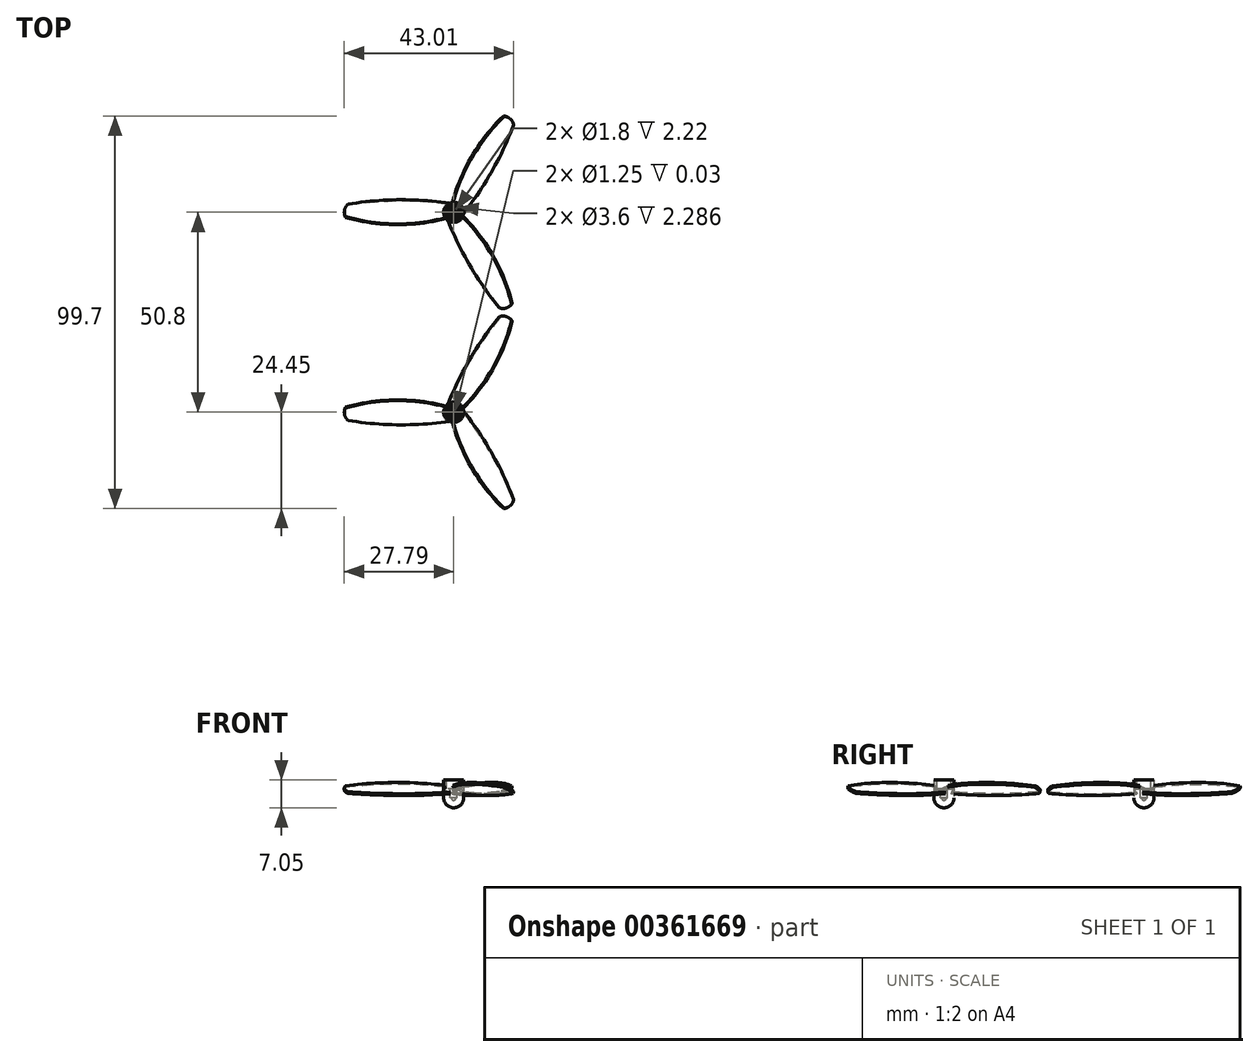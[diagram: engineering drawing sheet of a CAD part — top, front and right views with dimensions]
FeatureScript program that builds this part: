
annotation { "Feature Type Name" : "Feature", "Feature Type Description" : "" }
export const myFeature = defineFeature(function(context is Context, id is Id, definition is map)
    precondition{}
    {
        {
            var Q0;
            Q0=qCreatedBy(makeId("Top.planeOp"),FACE);
            var sketch = newSketch(context, id + "F0", { "sketchPlane" : qUnion([Q0])});
            skCircle(sketch, "E0", {"center": v(0, 0) * mm, "radius": 0.63 * mm});
            skCircle(sketch, "E1", {"center": v(0, 0) * mm, "radius": 1.5 * mm});
            skCircle(sketch, "E2.0", {"center": v(0, 0) * mm, "radius": 2.55 * mm});
            skArc(sketch, "E3", {"start": v(-1.98, 1.6) * mm, "mid": v(-14.75, 3.36) * mm, "end": v(-27.48, 1.31) * mm});
            skArc(sketch, "E4", {"start": v(-27.48, 1.31) * mm, "mid": v(-27.74, -0.54) * mm, "end": v(-26.84, -2.17) * mm});
            skArc(sketch, "E5", {"start": v(-26.84, -2.17) * mm, "mid": v(-13.84, -3.4) * mm, "end": v(-0.82, -2.42) * mm});
            skSolve(sketch);
        }
        {
            var Q0;
            Q0=makeQuery(id+"F0.imprint","IMPRINT",FACE,{"disambiguationData":[TD([[makeQuery(id+"F0.imprint","IMPRINT",EDGE,{"derivedFrom":sQuery(id+"F0.wireOp",EDGE,"E1")}),-1.0]])]});
            extrude(context, id + "F1", {"entities" : qUnion([Q0]), "endBound" : BoundingType.SYMMETRIC, "depth" : 4.5 * mm});
        }
        {
            var Q0;
            Q0=makeQuery(id+"F0.imprint","IMPRINT",FACE,{"disambiguationData":[TD([[makeQuery(id+"F0.imprint","IMPRINT",EDGE,{"derivedFrom":sQuery(id+"F0.wireOp",EDGE,"E0")}),-1.0]])]});
            extrude(context, id + "F2", {"entities" : qUnion([Q0]), "operationType" : NewBodyOperationType.ADD, "oppositeDirection" : true, "depth" : 2.25 * mm});
        }
        {
            var Q0;
            {var subQ0=sQuery(id+"F0.wireOp",EDGE,"E1");Q0=makeQuery(id+"F2.boolean.opBoolean","MERGE",FACE,{"derivedFrom":[makeQuery(id+"F1.opExtrude","CAP_FACE",FACE,{"disambiguationData":[OSD([subQ0,sQuery(id+"F0.wireOp",EDGE,"E2.0")])],"isStart":true}),makeQuery(id+"F2.opExtrude","CAP_FACE",FACE,{"disambiguationData":[OSD([sQuery(id+"F0.wireOp",EDGE,"E0"),subQ0])],"isStart":false})]});}
            var sketch = newSketch(context, id + "F3", { "sketchPlane" : qUnion([Q0])});
            skLineSegment(sketch, "E6", {"start": v(0, 2.55) * mm, "end": v(0, -2.55) * mm});
            skArc(sketch, "E7", {"start": v(0, -2.55) * mm, "mid": v(2.55, 0) * mm, "end": v(0, 2.55) * mm});
            skSolve(sketch);
        }
        {
            var Q0;
            {var subQ0=sQuery(id+"F3.wireOp",EDGE,"E7");Q0=makeQuery(id+"F3.imprint","IMPRINT",FACE,{"disambiguationData":[TD([[makeQuery(id+"F3.imprint","IMPRINT",EDGE,{"derivedFrom":subQ0}),-1.0]])]});}
            var Q1;
            Q1=sQuery(id+"F3.wireOp",EDGE,"E6");
            revolve(context, id + "F4", {"operationType" : NewBodyOperationType.ADD, "entities" : qUnion([Q0]), "axis" : qUnion([Q1]), "revolveType" : RevolveType.ONE_DIRECTION, "angle" : 180 * degree});
        }
        {
            var Q0;
            {var subQ0=sQuery(id+"F0.wireOp",EDGE,"E3");Q0=makeQuery(id+"F0.imprint","IMPRINT",FACE,{"disambiguationData":[TD([[makeQuery(id+"F0.imprint","IMPRINT",EDGE,{"derivedFrom":subQ0}),1.0]])]});}
            extrude(context, id + "F5", {"entities" : qUnion([Q0]), "endBound" : BoundingType.SYMMETRIC, "depth" : 0.5 * mm});
        }
        {
            var Q0;
            Q0=qCreatedBy(makeId("Top.planeOp"),FACE);
            var sketch = newSketch(context, id + "F6", { "sketchPlane" : qUnion([Q0])});
            skLineSegment(sketch, "E8", {"start": v(7.03, 0) * mm, "end": v(-6.93, 0) * mm});
            skSolve(sketch);
        }
        {
            var Q0;
            Q0=makeQuery(id+"F5.opExtrude","SWEPT_BODY",BODY,{"disambiguationData":[OSD([sQuery(id+"F0.wireOp",EDGE,"E2.0"),sQuery(id+"F0.wireOp",EDGE,"E3"),sQuery(id+"F0.wireOp",EDGE,"E4"),sQuery(id+"F0.wireOp",EDGE,"E5")])]});
            var Q1;
            Q1=sQuery(id+"F6.wireOp",EDGE,"E8");
            transform(context, id + "F7", {"entities" : qUnion([Q0]), "transformType" : TransformType.ROTATION, "transformAxis" : qUnion([Q1]), "angle" : 25 * degree, "oppositeDirection" : true, "makeCopy" : false});
        }
        {
            var Q0;
            Q0=makeQuery(id+"F5.opExtrude","SWEPT_BODY",BODY,{"disambiguationData":[OSD([sQuery(id+"F0.wireOp",EDGE,"E2.0"),sQuery(id+"F0.wireOp",EDGE,"E3"),sQuery(id+"F0.wireOp",EDGE,"E4"),sQuery(id+"F0.wireOp",EDGE,"E5")])]});
            var Q1;
            Q1=sQuery(id+"F0.wireOp",EDGE,"E0");
            circularPattern(context, id + "F8", {"entities" : qUnion([Q0]), "axis" : qUnion([Q1]), "angle" : 360 * degree, "instanceCount" : 3, "equalSpace" : true});
        }
        {
            var Q0;
            Q0=makeQuery(id+"F8.opPattern","COPY",BODY,{"derivedFrom":makeQuery(id+"F5.opExtrude","SWEPT_BODY",BODY,{"disambiguationData":[OSD([sQuery(id+"F0.wireOp",EDGE,"E2.0"),sQuery(id+"F0.wireOp",EDGE,"E3"),sQuery(id+"F0.wireOp",EDGE,"E4"),sQuery(id+"F0.wireOp",EDGE,"E5")])]}),"instanceName":"1"});
            var Q1;
            Q1=makeQuery(id+"F8.opPattern","COPY",BODY,{"derivedFrom":makeQuery(id+"F5.opExtrude","SWEPT_BODY",BODY,{"disambiguationData":[OSD([sQuery(id+"F0.wireOp",EDGE,"E2.0"),sQuery(id+"F0.wireOp",EDGE,"E3"),sQuery(id+"F0.wireOp",EDGE,"E4"),sQuery(id+"F0.wireOp",EDGE,"E5")])]}),"instanceName":"2"});
            var Q2;
            Q2=makeQuery(id+"F5.opExtrude","SWEPT_BODY",BODY,{"disambiguationData":[OSD([sQuery(id+"F0.wireOp",EDGE,"E2.0"),sQuery(id+"F0.wireOp",EDGE,"E3"),sQuery(id+"F0.wireOp",EDGE,"E4"),sQuery(id+"F0.wireOp",EDGE,"E5")])]});
            var Q3;
            Q3=makeQuery(id+"F1.opExtrude","SWEPT_BODY",BODY,{"disambiguationData":[OSD([sQuery(id+"F0.wireOp",EDGE,"E1"),sQuery(id+"F0.wireOp",EDGE,"E2.0")])]});
            var Q4;
            Q4=qCreatedBy(makeId("Front.planeOp"),FACE);
            transform(context, id + "F9", {"entities" : qUnion([Q0, Q1, Q2, Q3]), "transformType" : TransformType.TRANSLATION_DISTANCE, "transformDirection" : qUnion([Q4]), "distance" : 25.4 * mm, "makeCopy" : false});
        }
        {
            var Q0;
            Q0=makeQuery(id+"F1.opExtrude","CAP_FACE",FACE,{"disambiguationData":[OSD([sQuery(id+"F0.wireOp",EDGE,"E1"),sQuery(id+"F0.wireOp",EDGE,"E2.0")])],"isStart":false});
            var sketch = newSketch(context, id + "F10", { "sketchPlane" : qUnion([Q0])});
            skCircle(sketch, "E9", {"center": v(0, -25.4) * mm, "radius": 0.9 * mm});
            skCircle(sketch, "E10", {"center": v(0, -25.4) * mm, "radius": 1.8 * mm});
            skSolve(sketch);
        }
        {
            var Q0;
            Q0=makeQuery(id+"F10.imprint","IMPRINT",FACE,{"disambiguationData":[TD([[makeQuery(id+"F10.imprint","IMPRINT",EDGE,{"derivedFrom":sQuery(id+"F10.wireOp",EDGE,"E9")}),1.0]])]});
            extrude(context, id + "F11", {"entities" : qUnion([Q0]), "operationType" : NewBodyOperationType.REMOVE, "oppositeDirection" : true, "depth" : 4.47 * mm});
        }
        {
            var Q0;
            Q0=makeQuery(id+"F10.imprint","IMPRINT",FACE,{"disambiguationData":[TD([[makeQuery(id+"F10.imprint","IMPRINT",EDGE,{"derivedFrom":sQuery(id+"F10.wireOp",EDGE,"E10")}),1.0]])]});
            extrude(context, id + "F12", {"entities" : qUnion([Q0]), "operationType" : NewBodyOperationType.REMOVE, "oppositeDirection" : true, "depth" : 2.3 * mm});
        }
        {
            var Q0;
            Q0=makeQuery(id+"F8.opPattern","COPY",BODY,{"derivedFrom":makeQuery(id+"F5.opExtrude","SWEPT_BODY",BODY,{"disambiguationData":[OSD([sQuery(id+"F0.wireOp",EDGE,"E2.0"),sQuery(id+"F0.wireOp",EDGE,"E3"),sQuery(id+"F0.wireOp",EDGE,"E4"),sQuery(id+"F0.wireOp",EDGE,"E5")])]}),"instanceName":"2"});
            var Q1;
            Q1=makeQuery(id+"F8.opPattern","COPY",BODY,{"derivedFrom":makeQuery(id+"F5.opExtrude","SWEPT_BODY",BODY,{"disambiguationData":[OSD([sQuery(id+"F0.wireOp",EDGE,"E2.0"),sQuery(id+"F0.wireOp",EDGE,"E3"),sQuery(id+"F0.wireOp",EDGE,"E4"),sQuery(id+"F0.wireOp",EDGE,"E5")])]}),"instanceName":"1"});
            var Q2;
            Q2=makeQuery(id+"F5.opExtrude","SWEPT_BODY",BODY,{"disambiguationData":[OSD([sQuery(id+"F0.wireOp",EDGE,"E2.0"),sQuery(id+"F0.wireOp",EDGE,"E3"),sQuery(id+"F0.wireOp",EDGE,"E4"),sQuery(id+"F0.wireOp",EDGE,"E5")])]});
            var Q3;
            Q3=makeQuery(id+"F1.opExtrude","SWEPT_BODY",BODY,{"disambiguationData":[OSD([sQuery(id+"F0.wireOp",EDGE,"E1"),sQuery(id+"F0.wireOp",EDGE,"E2.0")])]});
            var Q4;
            Q4=qCreatedBy(makeId("Front.planeOp"),FACE);
            mirror(context, id + "F13", {"entities" : qUnion([Q0, Q1, Q2, Q3]), "mirrorPlane" : qUnion([Q4])});
        }
    });
